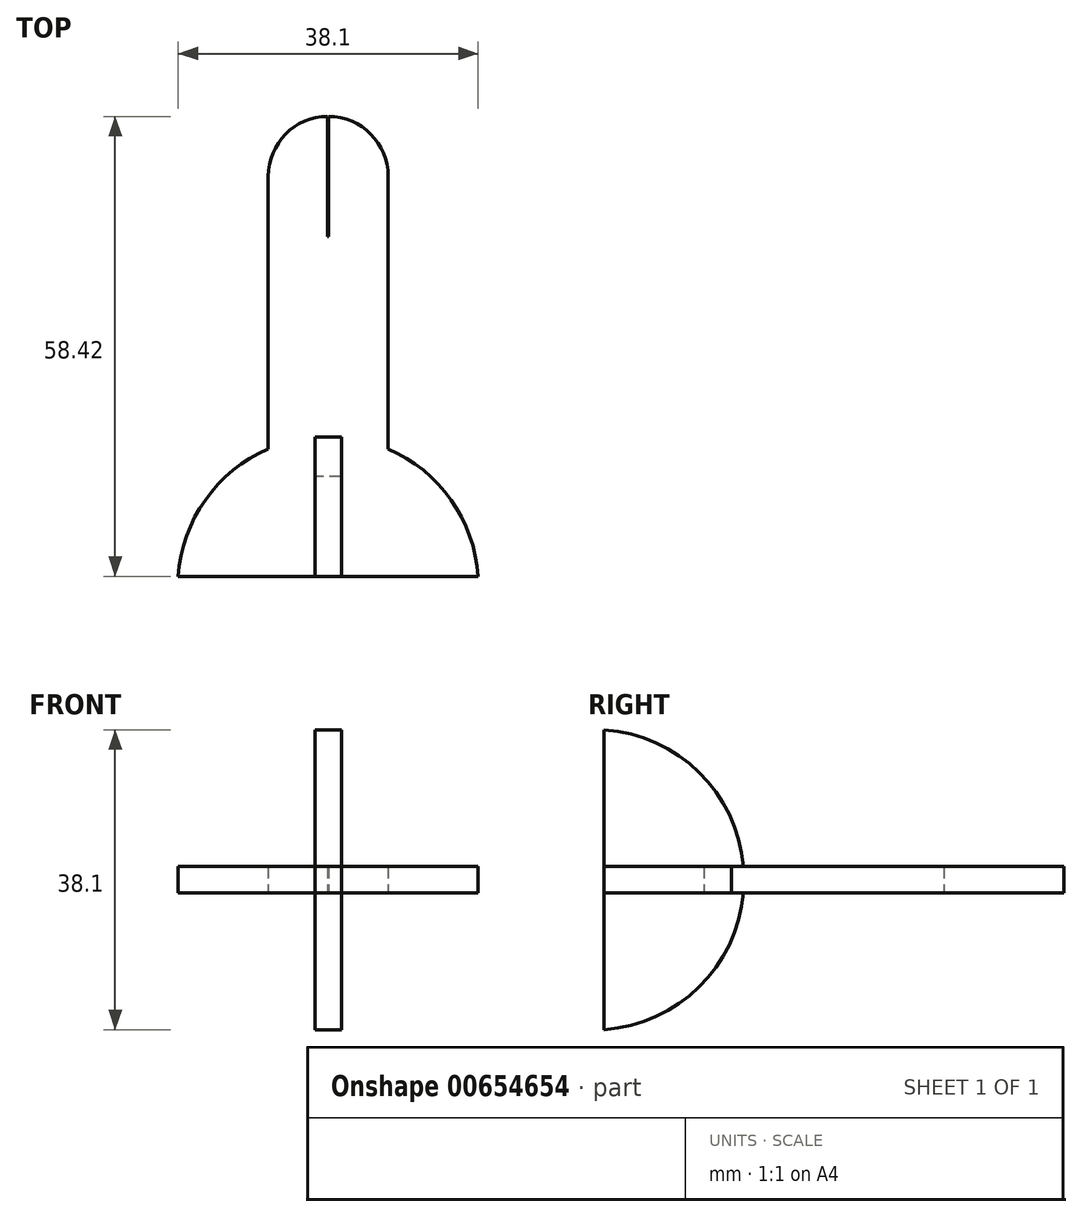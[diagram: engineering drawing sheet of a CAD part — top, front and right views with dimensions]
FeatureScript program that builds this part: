
annotation { "Feature Type Name" : "Feature", "Feature Type Description" : "" }
export const myFeature = defineFeature(function(context is Context, id is Id, definition is map)
    precondition{}
    {
        {
            var Q0;
            Q0=qCreatedBy(makeId("Top.planeOp"),FACE);
            var sketch = newSketch(context, id + "F0", { "sketchPlane" : qUnion([Q0])});
            skLineSegment(sketch, "E0", {"start": v(0, 0) * mm, "end": v(19.05, 0) * mm});
            skLineSegment(sketch, "E1", {"start": v(0, 0) * mm, "end": v(0, 17.78) * mm});
            skLineSegment(sketch, "E2.MirrorCS", {"start": v(0, 0) * mm, "end": v(-19.05, 0) * mm});
            skArc(sketch, "E3", {"start": v(19.05, 0) * mm, "mid": v(0, 17.78) * mm, "end": v(-19.05, 0) * mm});
            skLineSegment(sketch, "E4", {"start": v(-1.7, 0) * mm, "end": v(-1.7, 12.7) * mm});
            skLineSegment(sketch, "E5.MirrorCS", {"start": v(1.7, 0) * mm, "end": v(1.7, 12.7) * mm});
            skLineSegment(sketch, "E6", {"start": v(1.7, 12.7) * mm, "end": v(-1.7, 12.7) * mm});
            skLineSegment(sketch, "E7", {"start": v(-7.62, 0) * mm, "end": v(-7.62, 50.8) * mm});
            skLineSegment(sketch, "E8.MirrorCS", {"start": v(7.62, 0) * mm, "end": v(7.62, 50.8) * mm});
            skCircle(sketch, "E9", {"center": v(0, 50.8) * mm, "radius": 7.62 * mm});
            skLineSegment(sketch, "E10.bottom", {"start": v(0.06, 58.42) * mm, "end": v(-0.06, 58.42) * mm});
            skLineSegment(sketch, "E10.top", {"start": v(0.06, 43.18) * mm, "end": v(-0.06, 43.18) * mm});
            skLineSegment(sketch, "E10.left", {"start": v(0.06, 58.42) * mm, "end": v(0.06, 43.18) * mm});
            skLineSegment(sketch, "E10.right", {"start": v(-0.06, 58.42) * mm, "end": v(-0.06, 43.18) * mm});
            skLineSegment(sketch, "E11", {"start": v(-0.06, 58.42) * mm, "end": v(-0.06, 63.76) * mm});
            skLineSegment(sketch, "E12", {"start": v(-0.06, 63.76) * mm, "end": v(0.06, 63.76) * mm});
            skLineSegment(sketch, "E13", {"start": v(0.06, 63.76) * mm, "end": v(0.06, 58.42) * mm});
            skLineSegment(sketch, "E14", {"start": v(-0.06, 50.8) * mm, "end": v(0.06, 50.8) * mm});
            skSolve(sketch);
        }
        {
            var Q0;
            {var subQ0=sQuery(id+"F0.wireOp",EDGE,"E4");Q0=makeQuery(id+"F0.imprint","IMPRINT",FACE,{"disambiguationData":[TD([[makeQuery(id+"F0.imprint","IMPRINT",EDGE,{"derivedFrom":subQ0}),1.0]])]});}
            var Q1;
            {var subQ0=sQuery(id+"F0.wireOp",EDGE,"E5.MirrorCS");Q1=makeQuery(id+"F0.imprint","IMPRINT",FACE,{"disambiguationData":[TD([[makeQuery(id+"F0.imprint","IMPRINT",EDGE,{"derivedFrom":subQ0}),-1.0]])]});}
            var Q2;
            {var subQ0=sQuery(id+"F0.wireOp",EDGE,"E3");var subQ1=sQuery(id+"F0.wireOp",EDGE,"E0");var subQ2=makeQuery(id+"F0.imprint","INTERSECT",VERTEX,{"derivedFrom":[subQ1,subQ0]});Q2=makeQuery(id+"F0.imprint","IMPRINT",FACE,{"disambiguationData":[TD([[makeQuery(id+"F0.imprint","IMPRINT",EDGE,{"disambiguationData":[TD([[subQ2,1.0]])],"derivedFrom":subQ1}),1.0]])]});}
            var Q3;
            {var subQ0=sQuery(id+"F0.wireOp",EDGE,"E3");var subQ1=sQuery(id+"F0.wireOp",EDGE,"E2.MirrorCS");var subQ2=makeQuery(id+"F0.imprint","INTERSECT",VERTEX,{"derivedFrom":[subQ1,subQ0]});Q3=makeQuery(id+"F0.imprint","IMPRINT",FACE,{"disambiguationData":[TD([[makeQuery(id+"F0.imprint","IMPRINT",EDGE,{"disambiguationData":[TD([[subQ2,1.0]])],"derivedFrom":subQ1}),-1.0]])]});}
            var Q4;
            {var subQ0=sQuery(id+"F0.wireOp",EDGE,"E9");var subQ1=makeQuery(id+"F0.imprint","INTERSECT",VERTEX,{"derivedFrom":[sQuery(id+"F0.wireOp",EDGE,"E8.MirrorCS"),subQ0]});Q4=makeQuery(id+"F0.imprint","IMPRINT",FACE,{"disambiguationData":[TD([[makeQuery(id+"F0.imprint","IMPRINT",EDGE,{"disambiguationData":[TD([[subQ1,1.0]])],"derivedFrom":subQ0}),1.0]])]});}
            var Q5;
            {var subQ0=sQuery(id+"F0.wireOp",EDGE,"E9");var subQ1=makeQuery(id+"F0.imprint","INTERSECT",VERTEX,{"derivedFrom":[sQuery(id+"F0.wireOp",EDGE,"E7"),subQ0]});Q5=makeQuery(id+"F0.imprint","IMPRINT",FACE,{"disambiguationData":[TD([[makeQuery(id+"F0.imprint","IMPRINT",EDGE,{"disambiguationData":[TD([[subQ1,-1.0]])],"derivedFrom":subQ0}),1.0]])]});}
            var Q6;
            {var subQ3=sQuery(id+"F0.wireOp",EDGE,"E3");var subQ5=makeQuery(id+"F0.imprint","INTERSECT",VERTEX,{"derivedFrom":[sQuery(id+"F0.wireOp",EDGE,"E1"),subQ3]});Q6=makeQuery(id+"F0.imprint","IMPRINT",FACE,{"disambiguationData":[TD([[makeQuery(id+"F0.imprint","IMPRINT",EDGE,{"disambiguationData":[TD([[subQ5,1.0]])],"derivedFrom":subQ3}),-1.0]])]});}
            extrude(context, id + "F1", {"entities" : qUnion([Q0, Q1, Q2, Q3, Q4, Q5, Q6]), "depth" : 3.4 * mm, "offsetDistance" : 25.4 * mm});
        }
        {
            var Q0;
            Q0=makeQuery(id+"F1.opExtrude","SWEPT_FACE",FACE,{"disambiguationData":[OSD([sQuery(id+"F0.wireOp",EDGE,"E4")])]});
            var sketch = newSketch(context, id + "F2", { "sketchPlane" : qUnion([Q0])});
            skLineSegment(sketch, "E15.0", {"start": v(0, 3.39) * mm, "end": v(12.7, 3.39) * mm});
            skLineSegment(sketch, "E16.0", {"start": v(12.7, 3.39) * mm, "end": v(12.7, 0) * mm});
            skLineSegment(sketch, "E17.0", {"start": v(0, 0) * mm, "end": v(12.7, 0) * mm});
            skLineSegment(sketch, "E18.0", {"start": v(0, 3.39) * mm, "end": v(0, 0) * mm});
            skLineSegment(sketch, "E19", {"start": v(0, 1.7) * mm, "end": v(0, -17.36) * mm});
            skPoint(sketch, "E19.endSnap0", {"position": v(0, 1.7) * mm});
            skLineSegment(sketch, "E20", {"start": v(0, 1.7) * mm, "end": v(17.78, 1.7) * mm});
            skLineSegment(sketch, "E21.MirrorCS", {"start": v(0, 1.7) * mm, "end": v(0, 20.74) * mm});
            skArc(sketch, "E22", {"start": v(0, -17.36) * mm, "mid": v(17.78, 1.7) * mm, "end": v(0, 20.74) * mm});
            skLineSegment(sketch, "E23", {"start": v(12.7, 3.39) * mm, "end": v(17.7, 3.39) * mm});
            skLineSegment(sketch, "E24", {"start": v(12.7, 0) * mm, "end": v(17.7, 0) * mm});
            skLineSegment(sketch, "E25", {"start": v(12.7, 0) * mm, "end": v(0, 0) * mm});
            skLineSegment(sketch, "E26", {"start": v(0, 0) * mm, "end": v(0, 3.39) * mm});
            skSolve(sketch);
        }
        {
            var Q0;
            {var subQ0=sQuery(id+"F2.wireOp",EDGE,"E21.MirrorCS");Q0=makeQuery(id+"F2.imprint","IMPRINT",FACE,{"disambiguationData":[TD([[makeQuery(id+"F2.imprint","IMPRINT",EDGE,{"derivedFrom":subQ0}),-1.0]])]});}
            var Q1;
            {var subQ0=sQuery(id+"F2.wireOp",EDGE,"E19");Q1=makeQuery(id+"F2.imprint","IMPRINT",FACE,{"disambiguationData":[TD([[makeQuery(id+"F2.imprint","IMPRINT",EDGE,{"derivedFrom":subQ0}),1.0]])]});}
            var Q2;
            {var subQ5=sQuery(id+"F2.wireOp",EDGE,"E25");Q2=makeQuery(id+"F2.imprint","IMPRINT",FACE,{"disambiguationData":[TD([[makeQuery(id+"F2.imprint","IMPRINT",EDGE,{"derivedFrom":subQ5}),1.0]])]});}
            var Q3;
            {var subQ5=sQuery(id+"F2.wireOp",EDGE,"E15.0");Q3=makeQuery(id+"F2.imprint","IMPRINT",FACE,{"disambiguationData":[TD([[makeQuery(id+"F2.imprint","IMPRINT",EDGE,{"derivedFrom":subQ5}),-1.0]])]});}
            extrude(context, id + "F3", {"entities" : qUnion([Q0, Q1, Q2, Q3]), "depth" : 3.4 * mm, "offsetDistance" : 25.4 * mm});
        }
    });
